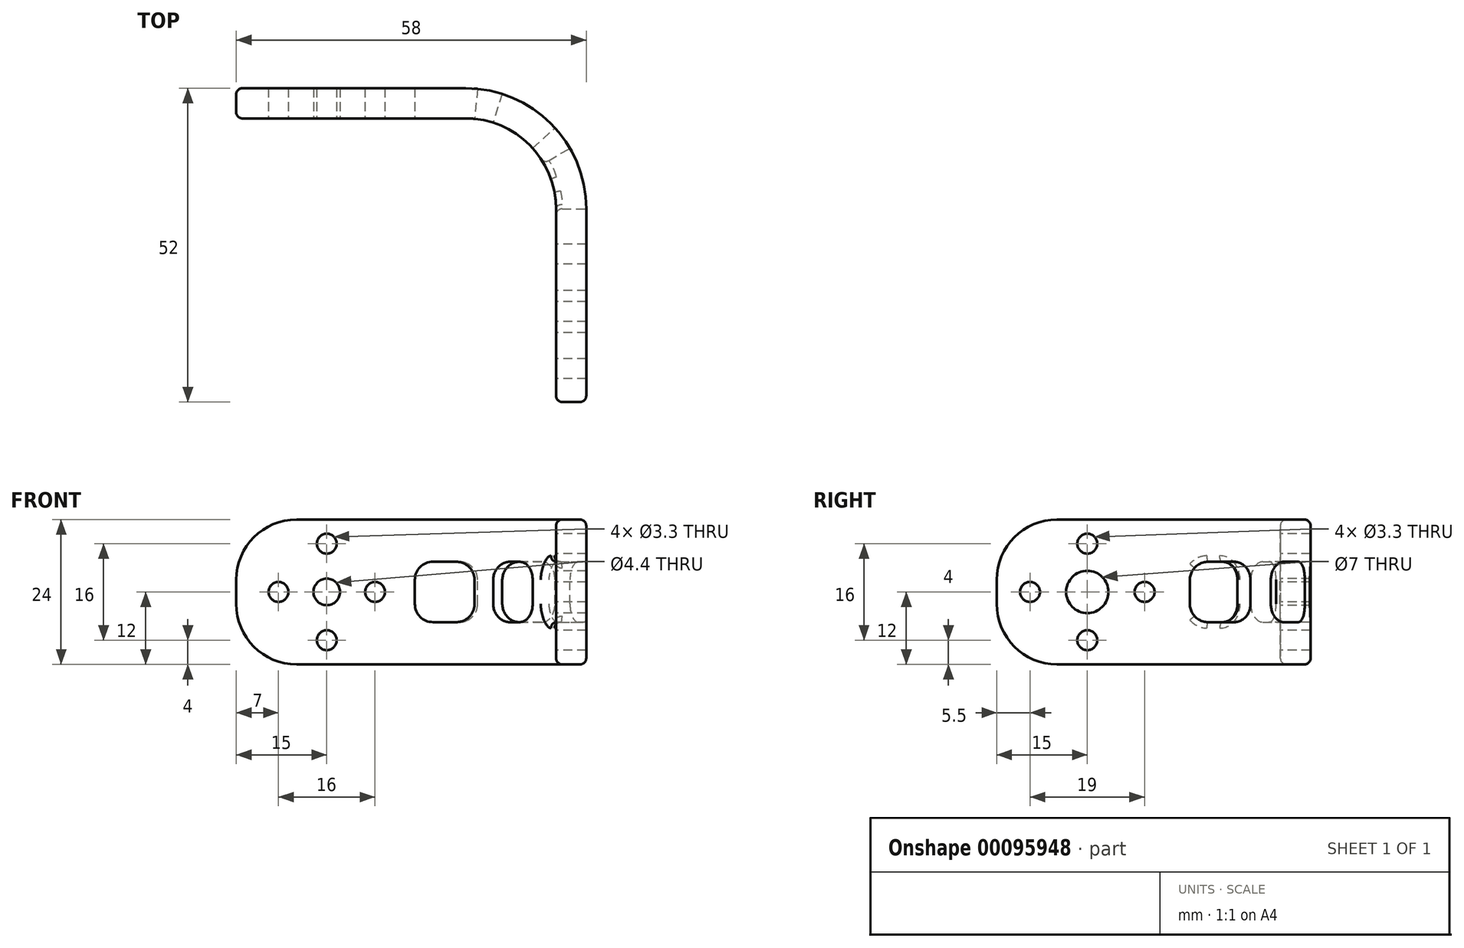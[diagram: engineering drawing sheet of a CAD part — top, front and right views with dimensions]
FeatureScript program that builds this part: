
annotation { "Feature Type Name" : "Feature", "Feature Type Description" : "" }
export const myFeature = defineFeature(function(context is Context, id is Id, definition is map)
    precondition{}
    {
        {
            var Q0;
            Q0=qCreatedBy(makeId("Top.planeOp"),FACE);
            var sketch = newSketch(context, id + "F0", { "sketchPlane" : qUnion([Q0])});
            skLineSegment(sketch, "E0", {"start": v(-15, 32) * mm, "end": v(23, 32) * mm});
            skLineSegment(sketch, "E1", {"start": v(38, 17) * mm, "end": v(38, -15) * mm});
            skLineSegment(sketch, "E2", {"start": v(38, -15) * mm, "end": v(43, -15) * mm});
            skLineSegment(sketch, "E3", {"start": v(43, -15) * mm, "end": v(43, 17) * mm});
            skLineSegment(sketch, "E4", {"start": v(23, 37) * mm, "end": v(-15, 37) * mm});
            skLineSegment(sketch, "E5", {"start": v(-15, 37) * mm, "end": v(-15, 32) * mm});
            skArc(sketch, "E6.filletArc", {"start": v(38, 17) * mm, "mid": v(33.6, 27.6) * mm, "end": v(23, 32) * mm});
            skArc(sketch, "E7.filletArc", {"start": v(43, 17) * mm, "mid": v(37.14, 31.14) * mm, "end": v(23, 37) * mm});
            skSolve(sketch);
        }
        {
            var Q0;
            Q0 = qSketchRegion(id + "F0", true);
            extrude(context, id + "F1", {"entities" : qUnion([Q0]), "depth" : 12 * mm, "hasSecondDirection" : true, "secondDirectionOppositeDirection" : true, "secondDirectionDepth" : 12 * mm});
        }
        {
            var Q0;
            Q0=makeQuery(id+"F1.opExtrude","SWEPT_FACE",FACE,{"disambiguationData":[OSD([sQuery(id+"F0.wireOp",EDGE,"E1")])]});
            var sketch = newSketch(context, id + "F2", { "sketchPlane" : qUnion([Q0])});
            skCircle(sketch, "E8", {"center": v(0, 0) * mm, "radius": 17.4 * mm, "construction": true});
            skCircle(sketch, "E9", {"center": v(0, 0) * mm, "radius": 3.5 * mm});
            skCircle(sketch, "E10", {"center": v(0, 8) * mm, "radius": 1.65 * mm});
            skCircle(sketch, "E11.1.0", {"center": v(-9.5, 0) * mm, "radius": 1.65 * mm});
            skCircle(sketch, "E11.2.0", {"center": v(0, -8) * mm, "radius": 1.65 * mm});
            skCircle(sketch, "E11.3.0", {"center": v(9.5, 0) * mm, "radius": 1.65 * mm});
            skLineSegment(sketch, "E12", {"start": v(0, 18.26) * mm, "end": v(0, -16.55) * mm, "construction": true});
            skLineSegment(sketch, "E13", {"start": v(22.4, 0) * mm, "end": v(-24.3, 0) * mm, "construction": true});
            skPoint(sketch, "E13.endSnap0", {"position": v(-17, 0) * mm});
            skSolve(sketch);
        }
        {
            var Q0;
            Q0 = qSketchRegion(id + "F2", true);
            extrude(context, id + "F3", {"entities" : qUnion([Q0]), "operationType" : NewBodyOperationType.REMOVE, "oppositeDirection" : true, "depth" : 5 * mm});
        }
        {
            var Q0;
            Q0=makeQuery(id+"F1.opExtrude","CAP_EDGE",EDGE,{"disambiguationData":[OSD([sQuery(id+"F0.wireOp",EDGE,"E5")])],"isStart":false});
            var Q1;
            Q1=makeQuery(id+"F1.opExtrude","CAP_EDGE",EDGE,{"disambiguationData":[OSD([sQuery(id+"F0.wireOp",EDGE,"E5")])],"isStart":true});
            var Q2;
            Q2=makeQuery(id+"F1.opExtrude","CAP_EDGE",EDGE,{"disambiguationData":[OSD([sQuery(id+"F0.wireOp",EDGE,"E2")])],"isStart":false});
            var Q3;
            Q3=makeQuery(id+"F1.opExtrude","CAP_EDGE",EDGE,{"disambiguationData":[OSD([sQuery(id+"F0.wireOp",EDGE,"E2")])],"isStart":true});
            fillet(context, id + "F4", {"entities" : qUnion([Q0, Q1, Q2, Q3]), "radius" : 10 * mm, "tangentPropagation" : true, "allowEdgeOverflow" : false});
        }
        {
            var Q0;
            Q0=makeQuery(id+"F1.opExtrude","CAP_VERTEX",VERTEX,{"disambiguationData":[OSD([sQuery(id+"F0.wireOp",EDGE,"E0"),sQuery(id+"F0.wireOp",EDGE,"E6.filletArc")])],"isStart":false});
            var Q1;
            {var subQ0=sQuery(id+"F0.wireOp",EDGE,"E5");Q1=makeQuery(id+"F4.opFillet","BLEND_VERTEX",VERTEX,{"blendedFrom":[makeQuery(id+"F1.opExtrude","CAP_EDGE",EDGE,{"disambiguationData":[OSD([subQ0])],"isStart":false}),makeQuery(id+"F1.opExtrude","SWEPT_FACE",FACE,{"disambiguationData":[OSD([sQuery(id+"F0.wireOp",EDGE,"E0")])]}),makeQuery(id+"F1.opExtrude","SWEPT_FACE",FACE,{"disambiguationData":[OSD([subQ0])]})],"blendedInto":[makeQuery(id+"F1.opExtrude","SWEPT_FACE",FACE,{"disambiguationData":[OSD([sQuery(id+"F0.wireOp",EDGE,"E0")])]}),makeQuery(id+"F1.opExtrude","SWEPT_FACE",FACE,{"disambiguationData":[OSD([subQ0])]})]});}
            var Q2;
            Q2=makeQuery(id+"F1.opExtrude","CAP_VERTEX",VERTEX,{"disambiguationData":[OSD([sQuery(id+"F0.wireOp",EDGE,"E0"),sQuery(id+"F0.wireOp",EDGE,"E6.filletArc")])],"isStart":true});
            cPlane(context, id + "F5", {"entities" : qUnion([Q0, Q1, Q2]), "cplaneType" : CPlaneType.THREE_POINT, "offset" : 150 * mm, "width" : 150 * mm, "height" : 150 * mm});
        }
        {
            var Q0;
            Q0=qCreatedBy(id+"F5.planeOp",FACE);
            var sketch = newSketch(context, id + "F6", { "sketchPlane" : qUnion([Q0])});
            skLineSegment(sketch, "E14", {"start": v(0, 21.33) * mm, "end": v(0, -20.01) * mm, "construction": true});
            skLineSegment(sketch, "E15", {"start": v(25.06, 0) * mm, "end": v(-19.8, 0) * mm, "construction": true});
            skCircle(sketch, "E16", {"center": v(0, 0) * mm, "radius": 17.4 * mm, "construction": true});
            skCircle(sketch, "E17", {"center": v(0, 0) * mm, "radius": 2.2 * mm});
            skCircle(sketch, "E18", {"center": v(0, 8) * mm, "radius": 1.65 * mm});
            skCircle(sketch, "E19.1.0", {"center": v(-8, 0) * mm, "radius": 1.65 * mm});
            skCircle(sketch, "E19.2.0", {"center": v(0, -8) * mm, "radius": 1.65 * mm});
            skCircle(sketch, "E19.3.0", {"center": v(8, 0) * mm, "radius": 1.65 * mm});
            skSolve(sketch);
        }
        {
            var Q0;
            Q0 = qSketchRegion(id + "F6", true);
            extrude(context, id + "F7", {"entities" : qUnion([Q0]), "operationType" : NewBodyOperationType.REMOVE, "depth" : 5 * mm});
        }
        {
            var Q0;
            Q0=makeQuery(id+"F1.opExtrude","CAP_EDGE",EDGE,{"disambiguationData":[OSD([sQuery(id+"F0.wireOp",EDGE,"E0")])],"isStart":true});
            var Q1;
            Q1=makeQuery(id+"F1.opExtrude","CAP_EDGE",EDGE,{"disambiguationData":[OSD([sQuery(id+"F0.wireOp",EDGE,"E7.filletArc")])],"isStart":true});
            fillet(context, id + "F8", {"entities" : qUnion([Q0, Q1]), "radius" : 1 * mm, "tangentPropagation" : true, "allowEdgeOverflow" : false});
        }
        {
            var Q0;
            Q0=qCreatedBy(makeId("Top.planeOp"),FACE);
            var sketch = newSketch(context, id + "F9", { "sketchPlane" : qUnion([Q0])});
            skLineSegment(sketch, "E20", {"start": v(23, 37) * mm, "end": v(14.6, 37) * mm});
            skLineSegment(sketch, "E21", {"start": v(14.6, 37) * mm, "end": v(14.6, 32) * mm});
            skLineSegment(sketch, "E22", {"start": v(14.6, 32) * mm, "end": v(23, 32) * mm});
            skLineSegment(sketch, "E23", {"start": v(23, 17) * mm, "end": v(47.93, 17) * mm, "construction": true});
            skLineSegment(sketch, "E24", {"start": v(23, 17) * mm, "end": v(40.1, 32.46) * mm, "construction": true});
            skLineSegment(sketch, "E25", {"start": v(23, 17) * mm, "end": v(43.95, 29.16) * mm, "construction": true});
            skLineSegment(sketch, "E26", {"start": v(23, 17) * mm, "end": v(24.98, 36.77) * mm, "construction": true});
            skLineSegment(sketch, "E27", {"start": v(23, 17) * mm, "end": v(29.29, 36.67) * mm, "construction": true});
            skLineSegment(sketch, "E28", {"start": v(38, 17) * mm, "end": v(43, 17) * mm});
            skLineSegment(sketch, "E29", {"start": v(23, 17) * mm, "end": v(23, 38.2) * mm, "construction": true});
            skArc(sketch, "E30", {"start": v(43, 17) * mm, "mid": v(42.31, 22.2) * mm, "end": v(40.3, 27.04) * mm});
            skArc(sketch, "E31", {"start": v(38, 17) * mm, "mid": v(37.48, 20.9) * mm, "end": v(35.97, 24.53) * mm});
            skLineSegment(sketch, "E32", {"start": v(14.6, 37) * mm, "end": v(25, 36.9) * mm, "construction": true});
            skLineSegment(sketch, "E33", {"start": v(29.1, 36.05) * mm, "end": v(37.83, 30.42) * mm, "construction": true});
            skLineSegment(sketch, "E34", {"start": v(40.3, 27.04) * mm, "end": v(43, 17) * mm, "construction": true});
            skLineSegment(sketch, "E35", {"start": v(25, 36.9) * mm, "end": v(24.5, 31.93) * mm});
            skLineSegment(sketch, "E36", {"start": v(29.1, 36.05) * mm, "end": v(27.57, 31.29) * mm});
            skLineSegment(sketch, "E37", {"start": v(34.12, 27.06) * mm, "end": v(37.83, 30.42) * mm});
            skLineSegment(sketch, "E38", {"start": v(35.97, 24.53) * mm, "end": v(40.3, 27.04) * mm});
            skArc(sketch, "E39.trimOffspring", {"start": v(25, 36.9) * mm, "mid": v(24, 36.98) * mm, "end": v(23, 37) * mm});
            skArc(sketch, "E40.trimOffspring", {"start": v(24.5, 31.93) * mm, "mid": v(23.75, 31.98) * mm, "end": v(23, 32) * mm});
            skArc(sketch, "E41.trimOffspring", {"start": v(37.83, 30.42) * mm, "mid": v(33.83, 33.81) * mm, "end": v(29.1, 36.05) * mm});
            skArc(sketch, "E42.trimOffspring", {"start": v(34.12, 27.06) * mm, "mid": v(31.12, 29.6) * mm, "end": v(27.57, 31.29) * mm});
            skSolve(sketch);
        }
        {
            var Q0;
            Q0 = qSketchRegion(id + "F9", true);
            extrude(context, id + "F10", {"entities" : qUnion([Q0]), "operationType" : NewBodyOperationType.REMOVE, "oppositeDirection" : true, "depth" : 5 * mm, "hasSecondDirection" : true, "secondDirectionOppositeDirection" : false, "secondDirectionDepth" : 5 * mm});
        }
        {
            var Q0;
            Q0=makeQuery(id+"F10.boolean.opBoolean","COPY",EDGE,{"derivedFrom":makeQuery(id+"F10.opExtrude","CAP_EDGE",EDGE,{"disambiguationData":[OSD([sQuery(id+"F9.wireOp",EDGE,"E21")])],"isStart":false})});
            var Q1;
            Q1=makeQuery(id+"F10.boolean.opBoolean","COPY",EDGE,{"derivedFrom":makeQuery(id+"F10.opExtrude","CAP_EDGE",EDGE,{"disambiguationData":[OSD([sQuery(id+"F9.wireOp",EDGE,"E35")])],"isStart":false})});
            var Q2;
            Q2=makeQuery(id+"F10.boolean.opBoolean","COPY",EDGE,{"derivedFrom":makeQuery(id+"F10.opExtrude","CAP_EDGE",EDGE,{"disambiguationData":[OSD([sQuery(id+"F9.wireOp",EDGE,"E36")])],"isStart":false})});
            var Q3;
            Q3=makeQuery(id+"F10.boolean.opBoolean","COPY",EDGE,{"derivedFrom":makeQuery(id+"F10.opExtrude","CAP_EDGE",EDGE,{"disambiguationData":[OSD([sQuery(id+"F9.wireOp",EDGE,"E21")])],"isStart":true})});
            var Q4;
            Q4=makeQuery(id+"F10.boolean.opBoolean","COPY",EDGE,{"derivedFrom":makeQuery(id+"F10.opExtrude","CAP_EDGE",EDGE,{"disambiguationData":[OSD([sQuery(id+"F9.wireOp",EDGE,"E35")])],"isStart":true})});
            var Q5;
            Q5=makeQuery(id+"F10.boolean.opBoolean","COPY",EDGE,{"derivedFrom":makeQuery(id+"F10.opExtrude","CAP_EDGE",EDGE,{"disambiguationData":[OSD([sQuery(id+"F9.wireOp",EDGE,"E36")])],"isStart":true})});
            var Q6;
            Q6=makeQuery(id+"F10.boolean.opBoolean","COPY",EDGE,{"derivedFrom":makeQuery(id+"F10.opExtrude","CAP_EDGE",EDGE,{"disambiguationData":[OSD([sQuery(id+"F9.wireOp",EDGE,"E37")])],"isStart":true})});
            var Q7;
            Q7=makeQuery(id+"F10.boolean.opBoolean","COPY",EDGE,{"derivedFrom":makeQuery(id+"F10.opExtrude","CAP_EDGE",EDGE,{"disambiguationData":[OSD([sQuery(id+"F9.wireOp",EDGE,"E37")])],"isStart":false})});
            var Q8;
            Q8=makeQuery(id+"F10.boolean.opBoolean","COPY",EDGE,{"derivedFrom":makeQuery(id+"F10.opExtrude","CAP_EDGE",EDGE,{"disambiguationData":[OSD([sQuery(id+"F9.wireOp",EDGE,"E38")])],"isStart":false})});
            var Q9;
            Q9=makeQuery(id+"F10.boolean.opBoolean","COPY",EDGE,{"derivedFrom":makeQuery(id+"F10.opExtrude","CAP_EDGE",EDGE,{"disambiguationData":[OSD([sQuery(id+"F9.wireOp",EDGE,"E38")])],"isStart":true})});
            var Q10;
            Q10=makeQuery(id+"F10.boolean.opBoolean","COPY",EDGE,{"derivedFrom":makeQuery(id+"F10.opExtrude","CAP_EDGE",EDGE,{"disambiguationData":[OSD([sQuery(id+"F9.wireOp",EDGE,"E28")])],"isStart":true})});
            var Q11;
            Q11=makeQuery(id+"F10.boolean.opBoolean","COPY",EDGE,{"derivedFrom":makeQuery(id+"F10.opExtrude","CAP_EDGE",EDGE,{"disambiguationData":[OSD([sQuery(id+"F9.wireOp",EDGE,"E28")])],"isStart":false})});
            fillet(context, id + "F11", {"entities" : qUnion([Q0, Q1, Q2, Q3, Q4, Q5, Q6, Q7, Q8, Q9, Q10, Q11]), "radius" : 3 * mm, "tangentPropagation" : true, "allowEdgeOverflow" : false});
        }
        {
            var Q0;
            Q0=makeQuery(id+"F10.boolean.opBoolean","COPY",EDGE,{"derivedFrom":makeQuery(id+"F10.opExtrude","CAP_EDGE",EDGE,{"disambiguationData":[OSD([sQuery(id+"F9.wireOp",EDGE,"E20")])],"isStart":false})});
            var Q1;
            Q1=makeQuery(id+"F10.boolean.opBoolean","COPY",EDGE,{"derivedFrom":makeQuery(id+"F10.opExtrude","CAP_EDGE",EDGE,{"disambiguationData":[OSD([sQuery(id+"F9.wireOp",EDGE,"E30")])],"isStart":false})});
            var Q2;
            Q2=makeQuery(id+"F10.boolean.opBoolean","COPY",EDGE,{"derivedFrom":makeQuery(id+"F10.opExtrude","CAP_EDGE",EDGE,{"disambiguationData":[OSD([sQuery(id+"F9.wireOp",EDGE,"E22")])],"isStart":false})});
            var Q3;
            Q3=makeQuery(id+"F10.boolean.opBoolean","COPY",EDGE,{"derivedFrom":makeQuery(id+"F10.opExtrude","CAP_EDGE",EDGE,{"disambiguationData":[OSD([sQuery(id+"F9.wireOp",EDGE,"E41.trimOffspring")])],"isStart":false})});
            var Q4;
            Q4=makeQuery(id+"F10.boolean.opBoolean","COPY",EDGE,{"derivedFrom":makeQuery(id+"F10.opExtrude","CAP_EDGE",EDGE,{"disambiguationData":[OSD([sQuery(id+"F9.wireOp",EDGE,"E42.trimOffspring")])],"isStart":false})});
            var Q5;
            Q5=makeQuery(id+"F10.boolean.opBoolean","MERGE",EDGE,{"derivedFrom":[makeQuery(id+"F1.opExtrude","SWEPT_EDGE",EDGE,{"disambiguationData":[OSD([sQuery(id+"F0.wireOp",EDGE,"E1"),sQuery(id+"F0.wireOp",EDGE,"E6.filletArc")])]}),makeQuery(id+"F10.opExtrude","SWEPT_EDGE",EDGE,{"disambiguationData":[OSD([sQuery(id+"F9.wireOp",EDGE,"E28"),sQuery(id+"F9.wireOp",EDGE,"E31")])]})]});
            fillet(context, id + "F12", {"entities" : qUnion([Q0, Q1, Q2, Q3, Q4, Q5]), "radius" : 1 * mm, "tangentPropagation" : true, "allowEdgeOverflow" : false});
        }
    });
